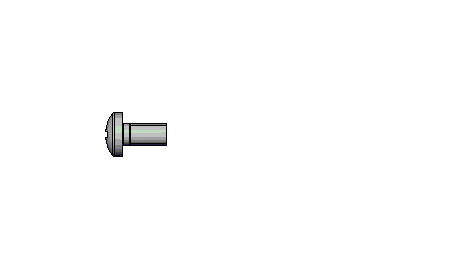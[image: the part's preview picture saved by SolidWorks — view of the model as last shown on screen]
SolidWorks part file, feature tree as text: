
SOLIDWORKS PART (.sldprt)
format: sldprt  version: not decoded by parser v0  size: 254,464 bytes
history: native  units: mm
features: sketch x5, plane x4, pattern_linear x4, cut_revolve x2, material x1, revolve x1, thread x1, fillet x1, pattern_circular x1 (+8 scaffold rows collapsed)
feature tree (28):
  scaffold x8  (default folders/planes/origin — collapsed)
  material  "Matériau <non spécifié>"
  plane  "Plane1"
  plane  "Plane2"
  plane  "Plane3"
  sketch  "BodySke"  dims[c1.Head_fillet_rad=3.6322mm c1.Head_crown_rad=6.5mm c2.Head_fillet_rad=0.36mm c2.D1=~7.099516mm c2.Head_ang=85.0deg c2.Oval_ht=2.3876mm c2.Head_ht=6.1976mm c2.Diameter=10.0mm c2.Length=76.2mm c2.Head_dia=20.0152mm c3.Head_dia=15.3924mm c3.Head_ht=8.509mm c3.Length=8.0mm c3.Head_side_ht=6.1722mm c4.Head_ht=5.1562mm c4.Head_dia=18.4912mm c5.Head_ht=3.1mm c5.Head_dia=8.0mm c5.Advance=0.7mm c5.Thread_nom=8.0mm c5.Thread_lim=~37.30625mm c5.Diameter=4.0mm]
  revolve  "Base-Revolve"  [1 undecoded]
  thread  "ThreadCosmetic"  Diameter=6.6mm Thread_length=6.6mm Thread_minor=3.22mm  [1 undecoded]
  fillet  "Fillet1"  Radius=0.2mm Head_dia=8mm Diameter=4mm
  sketch  "Sketch3"  dims[Cross_dia=4.3mm D1=2.15mm Cross_width=1.03mm D2=0.515mm]
  plane  "Plane4"  Offset=2.34mm Cross_depth=2.34mm
  sketch  "Sketch4"  dims[D1=1.03mm D2=~1.966638mm D3=0.515mm D4=~0.983319mm]
  pattern_circular  "RecPat"  Count=2 Angle=90deg
  sketch  "RecCorSke"  dims[c1.Diameter=1.702mm c1.Depth=2.34mm c1.D1=~7.118754mm c1.Draft_angle=4.0deg c2.D1=3.175mm c2.Bottom_angle=18.0deg]
  cut_revolve  "RecessCore"  Angle=360deg
  sketch  "ThdSchSke"  dims[c1.Thread_minor=~1.03886mm c1.Diameter=~1.413535mm c1.Start=~0.988134mm c1.D4=~4.446753mm c1.Vee=60.0deg c2.Thread_minor=~1.03886mm c2.Start=~2.540025mm c2.D1=~0.108159mm c2.D2=~0.108159mm c3.D1=~0.216319mm c3.SideAngle=55.0deg c3.D2=~0.216319mm c3.VeeAngle=70.0deg c3.Thread_minor=3.22mm c3.Overcut=5.0mm c3.Diameter=4.0mm c3.D6=~8.326268mm c4.D1=~8.326268mm c5.D1=90.0deg c5.Start=11.1125mm c6.Start=~44.450025mm c7.Start=4.5mm]
  cut_revolve  "ThreadSchematic"  Angle=360deg
  pattern_linear  "ThdSchPat"  Count1=11 Count2=1 Spacing1=0.66mm Spacing2=50mm Num_threads=11 Advance=0.66mm
  pattern_linear  "ConfigurationName"  Spacing1=0 CopiedFlag=0  [1 undecoded]
  pattern_linear  "PartNumberID"  [2 undecoded]
  pattern_linear  "ConfigurationName"  Spacing1=0 CopiedFlag=0  [1 undecoded]
decode coverage: 13 of 15 modeling features carry decoded parameters
note: ~ marks probable driven/reference dimensions
note: 6 parameter values undecoded
note: suppression state not decoded; provenance and decode notes live in map.json
